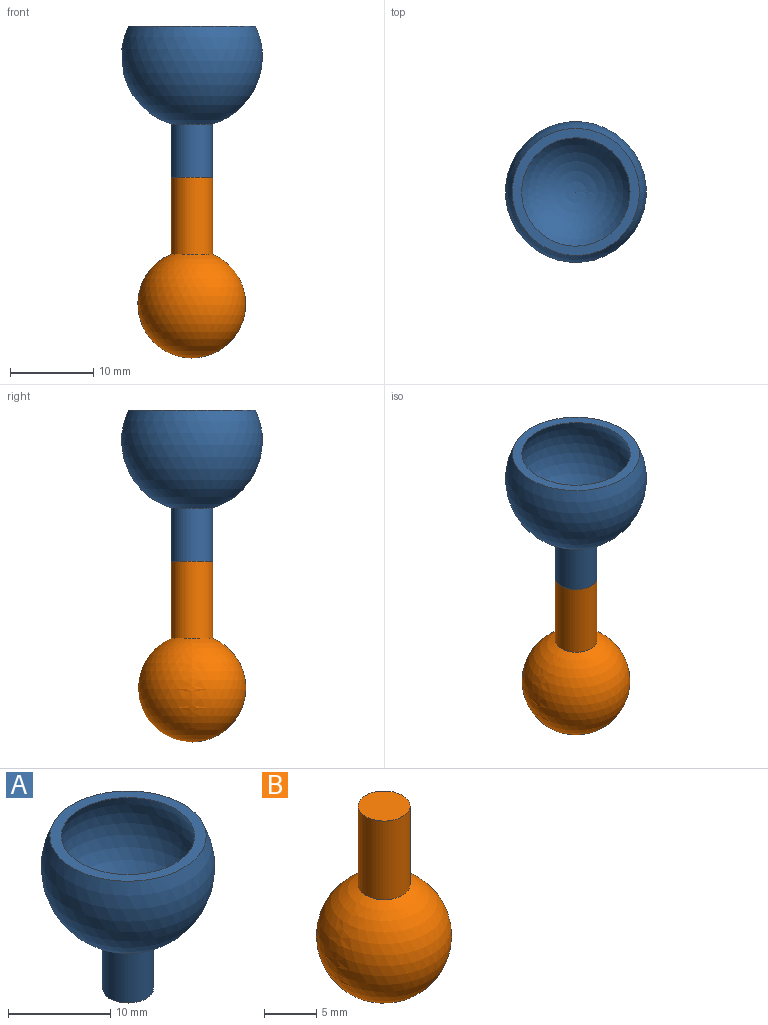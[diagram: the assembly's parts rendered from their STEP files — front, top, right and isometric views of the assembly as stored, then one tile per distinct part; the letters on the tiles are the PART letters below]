
ASSEMBLY  parts=2 mates=1
PART A: 5 faces, bbox 17x17x18.2 mm
  f0: cylinder r=2.5mm len=6.43mm, axis (0,0,1), area 101mm2, adj f1,f4
  f1: plane 5x5mm, normal (0,0,-1), area 19.6mm2, adj f0
  f2: sphere r=7.5mm, area 527.5mm2, adj f3
  f3: plane 15.31x15.31mm, normal (0,0,1), area 50.3mm2, adj f2,f4
  f4: sphere r=8.5mm, area 631.1mm2, adj f0,f3
PART B: 3 faces, bbox 13x13x21.7 mm
  f0: plane 5x5mm, normal (0,0,1), area 19.6mm2, adj f1
  f1: cylinder r=2.5mm len=9.25mm, axis (0,0,-1), area 145.3mm2, adj f0,f2
  f2: sphere r=6.5mm, area 510.5mm2, adj f1
PLACE A t=(-2.16,0.47,30.9)mm fixed
PLACE B t=(-2.16,0.47,1.1)mm
MATE fastened A.f0 <-> B.f1  axis (0,0,-1) through (-2.16,0.47,16.34)mm
